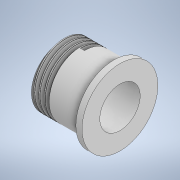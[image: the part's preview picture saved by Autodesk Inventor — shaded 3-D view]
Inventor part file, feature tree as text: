
AUTODESK INVENTOR PART (.ipt)
format: ipt  version: 2021.1 (Build 251245010, 245A)  size: 356,352 bytes
history: native  units: in
note: dims shown in document units (in); Inventor stores cm internally (conversion verified against a paired STEP export)
features: sketch x2, revolve x1, helix x1
ambient origin geometry x8: Origin, YZ Plane, XZ Plane, XY Plane, X Axis, Y Axis, Z Axis, Center Point
bodies: Solid1 (feature_tree)
feature tree (4):
  revolve  "Revolution1"  [1 undecoded]
  helix  "Coil1"  [1 undecoded]
  sketch  "Sketch2"  dims[d0=0.725in d1=0.3864in d2=0.118in]
  sketch  "Sketch4"  dims[d3=0.75in d4=90.0deg d5=0.6in d6=0.25in d10=60.0deg d11=0.0097in d12=60.0deg d13=60.0deg d15=0.1in d16=0.2in d17=0.05in d18=0.6042in d19=0.542in d20=30.0deg d21=0.1in d22=0.5in d23=0.3937in d24=0.0in d25=90.0deg d26=90.0deg d27=0.0in d28=0.0in]
note: 2 required parameter values undecoded (feature->parameter linkage not recoverable at this tier; creation-order binding heuristic only, values carry confidence <= 0.55)